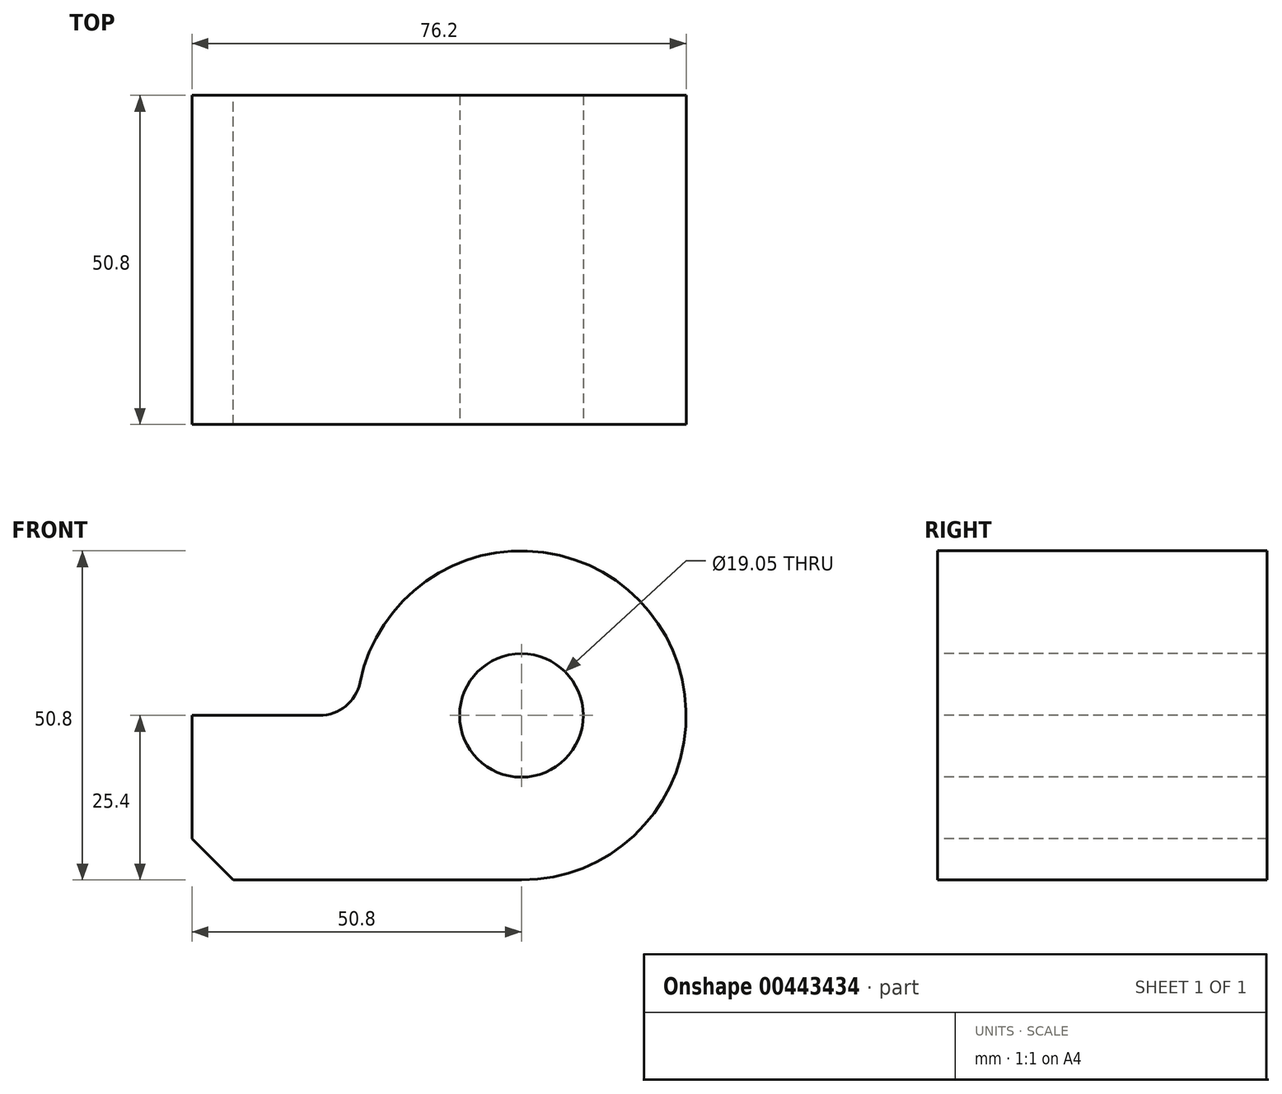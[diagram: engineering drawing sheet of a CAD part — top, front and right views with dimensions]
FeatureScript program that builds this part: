
annotation { "Feature Type Name" : "Feature", "Feature Type Description" : "" }
export const myFeature = defineFeature(function(context is Context, id is Id, definition is map)
    precondition{}
    {
        {
            var Q0;
            Q0=qCreatedBy(makeId("Front.planeOp"),FACE);
            var sketch = newSketch(context, id + "F0", { "sketchPlane" : qUnion([Q0])});
            skLineSegment(sketch, "E0.bottom", {"start": v(0, 0) * mm, "end": v(50.8, 0) * mm});
            skLineSegment(sketch, "E0.top", {"start": v(0, 25.4) * mm, "end": v(25.4, 25.4) * mm});
            skLineSegment(sketch, "E0.left", {"start": v(0, 0) * mm, "end": v(0, 25.4) * mm});
            skArc(sketch, "E1", {"start": v(50.8, 0) * mm, "mid": v(68.76, 43.36) * mm, "end": v(25.4, 25.4) * mm});
            skCircle(sketch, "E2", {"center": v(50.8, 25.4) * mm, "radius": 9.53 * mm});
            skSolve(sketch);
        }
        {
            var Q0;
            Q0 = qSketchRegion(id + "F0", true);
            extrude(context, id + "F1", {"entities" : qUnion([Q0]), "oppositeDirection" : true, "depth" : 50.8 * mm});
        }
        {
            var Q0;
            Q0=makeQuery(id+"F1.opExtrude","SWEPT_EDGE",EDGE,{"disambiguationData":[OSD([sQuery(id+"F0.wireOp",EDGE,"E0.top"),sQuery(id+"F0.wireOp",EDGE,"E1")])]});
            fillet(context, id + "F2", {"entities" : qUnion([Q0]), "radius" : 6.35 * mm, "tangentPropagation" : true, "allowEdgeOverflow" : false});
        }
        {
            var Q0;
            Q0=makeQuery(id+"F1.opExtrude","SWEPT_EDGE",EDGE,{"disambiguationData":[OSD([sQuery(id+"F0.wireOp",EDGE,"E0.bottom"),sQuery(id+"F0.wireOp",EDGE,"E0.left")])]});
            chamfer(context, id + "F3", {"entities" : qUnion([Q0]), "width" : 6.35 * mm, "tangentPropagation" : true});
        }
    });
